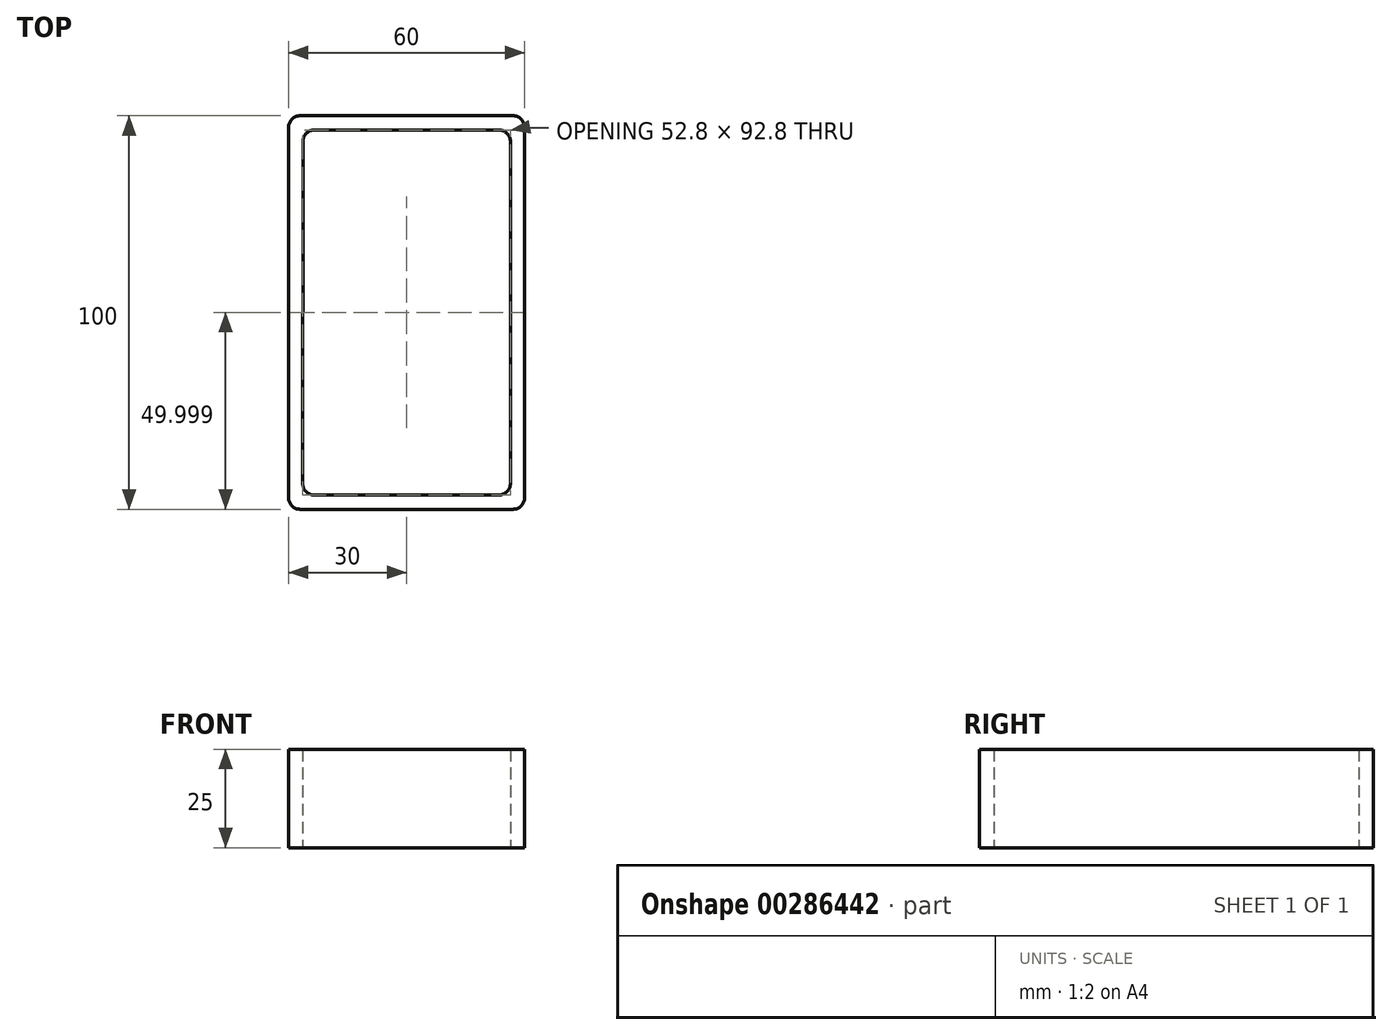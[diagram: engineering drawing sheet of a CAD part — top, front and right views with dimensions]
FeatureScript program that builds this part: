
annotation { "Feature Type Name" : "Feature", "Feature Type Description" : "" }
export const myFeature = defineFeature(function(context is Context, id is Id, definition is map)
    precondition{}
    {
        {
            var Q0;
            Q0=qCreatedBy(makeId("Top.planeOp"),FACE);
            var sketch = newSketch(context, id + "F0", { "sketchPlane" : qUnion([Q0])});
            skLineSegment(sketch, "E0", {"start": v(-37.16, 68.67) * mm, "end": v(16.84, 68.67) * mm});
            skLineSegment(sketch, "E1", {"start": v(19.84, 65.67) * mm, "end": v(19.84, -28.33) * mm});
            skLineSegment(sketch, "E2", {"start": v(-40.16, 65.67) * mm, "end": v(-40.16, -28.33) * mm});
            skLineSegment(sketch, "E3", {"start": v(-37.16, -31.33) * mm, "end": v(16.84, -31.33) * mm});
            skPoint(sketch, "E4.end.orphan", {"position": v(-34.97, -27.73) * mm});
            skPoint(sketch, "E5.start.orphan", {"position": v(-36.5, 65.07) * mm});
            skPoint(sketch, "E6.end.orphan", {"position": v(14.12, -27.73) * mm});
            skPoint(sketch, "E7.end.orphan", {"position": v(14.84, 65.07) * mm});
            skLineSegment(sketch, "E8", {"start": v(-33.5, 65.07) * mm, "end": v(13.24, 65.07) * mm});
            skLineSegment(sketch, "E9", {"start": v(16.24, 62.07) * mm, "end": v(16.24, -24.73) * mm});
            skLineSegment(sketch, "E10", {"start": v(13.24, -27.73) * mm, "end": v(-33.56, -27.73) * mm});
            skLineSegment(sketch, "E11", {"start": v(-36.56, -24.73) * mm, "end": v(-36.5, 62.07) * mm});
            skPoint(sketch, "E12.start.orphan", {"position": v(19.84, 65.07) * mm});
            skPoint(sketch, "E13.start.orphan", {"position": v(-40.16, 65.07) * mm});
            skPoint(sketch, "E14.start.orphan", {"position": v(-40.16, -27.73) * mm});
            skPoint(sketch, "E15.start.orphan", {"position": v(19.84, -27.73) * mm});
            skPoint(sketch, "E16.visualSharp", {"position": v(19.84, -31.33) * mm});
            skArc(sketch, "E16.filletArc", {"start": v(16.84, -31.33) * mm, "mid": v(18.96, -30.45) * mm, "end": v(19.84, -28.33) * mm});
            skPoint(sketch, "E17.visualSharp", {"position": v(-40.16, -31.33) * mm});
            skArc(sketch, "E17.filletArc", {"start": v(-40.16, -28.33) * mm, "mid": v(-39.28, -30.45) * mm, "end": v(-37.16, -31.33) * mm});
            skPoint(sketch, "E18.visualSharp", {"position": v(-36.56, -27.73) * mm});
            skArc(sketch, "E18.filletArc", {"start": v(-36.56, -24.73) * mm, "mid": v(-35.68, -26.85) * mm, "end": v(-33.56, -27.73) * mm});
            skPoint(sketch, "E19.visualSharp", {"position": v(16.24, -27.73) * mm});
            skArc(sketch, "E19.filletArc", {"start": v(13.24, -27.73) * mm, "mid": v(15.36, -26.85) * mm, "end": v(16.24, -24.73) * mm});
            skPoint(sketch, "E20.visualSharp", {"position": v(19.84, 68.67) * mm});
            skArc(sketch, "E20.filletArc", {"start": v(19.84, 65.67) * mm, "mid": v(18.96, 67.8) * mm, "end": v(16.84, 68.67) * mm});
            skPoint(sketch, "E21.visualSharp", {"position": v(16.24, 65.07) * mm});
            skArc(sketch, "E21.filletArc", {"start": v(16.24, 62.07) * mm, "mid": v(15.36, 64.2) * mm, "end": v(13.24, 65.07) * mm});
            skArc(sketch, "E22.filletArc", {"start": v(-33.5, 65.07) * mm, "mid": v(-35.63, 64.2) * mm, "end": v(-36.5, 62.07) * mm});
            skPoint(sketch, "E23.visualSharp", {"position": v(-40.16, 68.67) * mm});
            skArc(sketch, "E23.filletArc", {"start": v(-37.16, 68.67) * mm, "mid": v(-39.28, 67.8) * mm, "end": v(-40.16, 65.67) * mm});
            skSolve(sketch);
        }
        {
            var Q0;
            Q0 = qSketchRegion(id + "F0", true);
            extrude(context, id + "F1", {"entities" : qUnion([Q0]), "depth" : 25 * mm});
        }
    });
